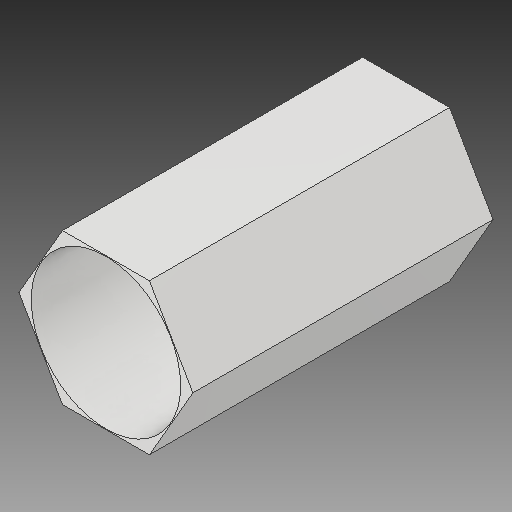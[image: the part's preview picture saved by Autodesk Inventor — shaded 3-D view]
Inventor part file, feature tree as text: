
AUTODESK INVENTOR PART (.ipt)
format: ipt  version: 2017 (Build 210142000, 142)  size: 97,792 bytes
history: native  units: in
note: dims shown in document units (in); Inventor stores cm internally (conversion verified against a paired STEP export)
features: extrude x1, sketch x1
ambient origin geometry x8: Origin, YZ Plane, XZ Plane, XY Plane, X Axis, Y Axis, Z Axis, Center Point
bodies: Solid1 (feature_tree)
feature tree (2):
  extrude  "Extrusion1"  Depth=1.0in TaperAngle=0.0deg
  sketch  "Sketch1"  dims[d0=0.498in d1=1.0in d2=0.0in]
